# Revit family: Caroma Cosmo Wall Basin
name_source: partatom
category: Plumbing Fixtures
revit_build: Autodesk Revit LT 2014 (Build: 20130308_1515(x64)
units: mm (PartAtom-declared; Revit-internal decimal feet)

## types (1)
- Cosmo - 3 Tap Holes
    1 Taphole = No
    3 Tapholes = Yes
    Assembly Code = D2010310
    CW Connection = No
    Default Elevation = 865 mm  [stored 2.83793 ft]
    Depth_ANZRS = 173 mm  [stored 0.567585 ft]
    Description = Caroma Cosmo Wall Basin
    HW Connection = No
    Length_ANZRS = 500 mm  [stored 1.64042 ft]
    Manufacturer = GWA Bathrooms & Kitchens
    Material_ANZRS = Porcelain-White-Caroma
    Model = 861535W
    ModifiedIssue_ANZRS = 20140916 $
    Pedestal = No
    Shroud = Yes
    Spout Penetration = 0 mm  [stored 0 ft]
    Tap Penetrations = 0 mm  [stored 0 ft]
    Type Comments = White Only, Overflow Only, Includes flush-ftting coloured plug and waste, optional pedestal shroud or bottle trap
    URL = http://www.caroma.com.au
    Vent Connection = No
    WFU = 1
    Waste = Metal-Chrome-Caroma
    Waste Connection = Yes
    Width_ANZRS = 440 mm  [stored 1.44357 ft]

note: [stored X ft] marks values corroborated as IEEE doubles in the binary element streams (Revit-internal decimal feet)

## geometry (parser evidence)
native form markers: Blend x20, Sweep x1
no freeform markers — native parametric forms only
